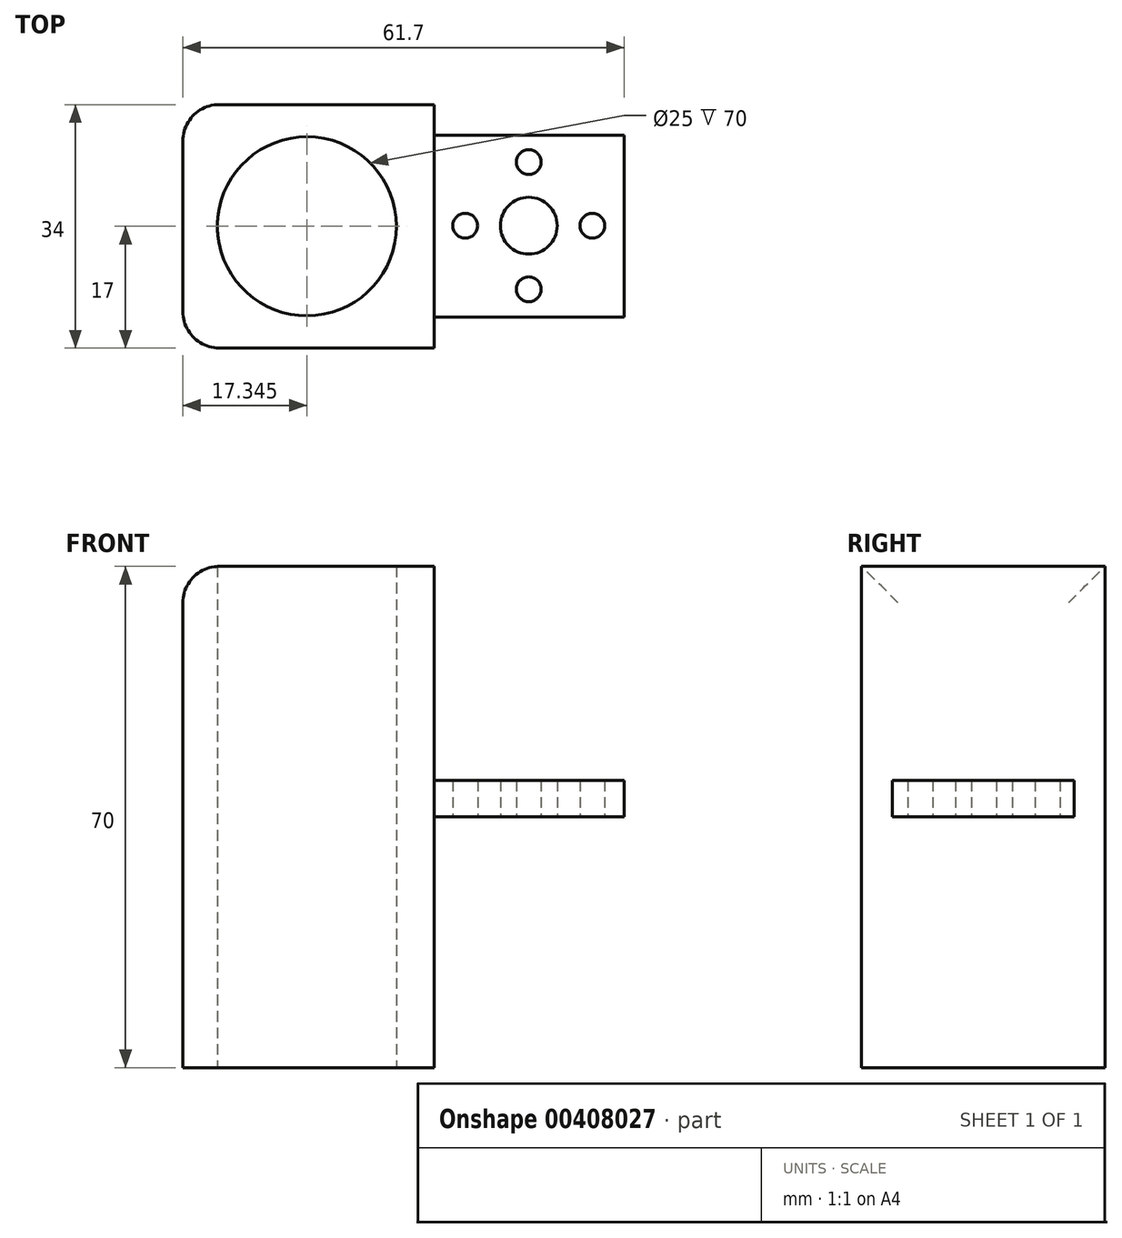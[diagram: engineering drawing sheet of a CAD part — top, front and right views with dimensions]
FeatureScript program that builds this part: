
annotation { "Feature Type Name" : "Feature", "Feature Type Description" : "" }
export const myFeature = defineFeature(function(context is Context, id is Id, definition is map)
    precondition{}
    {
        {
            var Q0;
            Q0=qCreatedBy(makeId("Top.planeOp"),FACE);
            var sketch = newSketch(context, id + "F0", { "sketchPlane" : qUnion([Q0])});
            skCircle(sketch, "E0", {"center": v(0, 0) * mm, "radius": 12.7 * mm});
            skLineSegment(sketch, "E1.bottom", {"start": v(12.38, 12.7) * mm, "end": v(42.86, 12.7) * mm});
            skLineSegment(sketch, "E1.top", {"start": v(12.38, -12.7) * mm, "end": v(42.86, -12.7) * mm});
            skLineSegment(sketch, "E1.right", {"start": v(42.86, 12.7) * mm, "end": v(42.86, -12.7) * mm});
            skCircle(sketch, "E2", {"center": v(29.5, 8.96) * mm, "radius": 1.74 * mm});
            skCircle(sketch, "E3", {"center": v(20.62, 0.08) * mm, "radius": 1.74 * mm});
            skCircle(sketch, "E4", {"center": v(38.38, 0.08) * mm, "radius": 1.74 * mm});
            skCircle(sketch, "E5", {"center": v(29.5, -8.8) * mm, "radius": 1.74 * mm});
            skCircle(sketch, "E6", {"center": v(29.5, 0.08) * mm, "radius": 3.97 * mm});
            skPoint(sketch, "E7", {"position": v(0, 12.7) * mm});
            skLineSegment(sketch, "E8", {"start": v(0, 12.7) * mm, "end": v(12.38, 12.7) * mm});
            skPoint(sketch, "E9", {"position": v(0, -12.7) * mm});
            skLineSegment(sketch, "E10", {"start": v(0, -12.7) * mm, "end": v(12.38, -12.7) * mm});
            skLineSegment(sketch, "E11", {"start": v(14.1, 12.7) * mm, "end": v(14.1, -12.7) * mm});
            skLineSegment(sketch, "E12.MirrorCS", {"start": v(0, 12.7) * mm, "end": v(-12.38, 12.7) * mm});
            skLineSegment(sketch, "E13.MirrorCS", {"start": v(-14.1, 12.7) * mm, "end": v(-14.1, -12.7) * mm});
            skLineSegment(sketch, "E14.MirrorCS", {"start": v(0, -12.7) * mm, "end": v(-12.38, -12.7) * mm});
            skLineSegment(sketch, "E15", {"start": v(-14.1, 12.7) * mm, "end": v(-12.38, 12.7) * mm});
            skLineSegment(sketch, "E16", {"start": v(-14.1, -12.7) * mm, "end": v(-12.38, -12.7) * mm});
            skLineSegment(sketch, "E17", {"start": v(14.1, 12.7) * mm, "end": v(14.1, 14.85) * mm});
            skLineSegment(sketch, "E18.MirrorCS", {"start": v(14.1, -12.7) * mm, "end": v(14.1, -14.85) * mm});
            skLineSegment(sketch, "E19", {"start": v(14.1, 14.85) * mm, "end": v(-14.1, 14.85) * mm});
            skLineSegment(sketch, "E20", {"start": v(-14.1, 14.85) * mm, "end": v(-14.1, 12.7) * mm});
            skLineSegment(sketch, "E21.MirrorCS", {"start": v(14.1, -14.85) * mm, "end": v(-14.1, -14.85) * mm});
            skLineSegment(sketch, "E22.MirrorCS", {"start": v(-14.1, -14.85) * mm, "end": v(-14.1, -12.7) * mm});
            skSolve(sketch);
        }
        {
            var Q0;
            {var subQ0=sQuery(id+"F0.wireOp",EDGE,"E1.right");Q0=makeQuery(id+"F0.imprint","IMPRINT",FACE,{"disambiguationData":[TD([[makeQuery(id+"F0.imprint","IMPRINT",EDGE,{"derivedFrom":subQ0}),-1.0]])]});}
            extrude(context, id + "F1", {"entities" : qUnion([Q0]), "depth" : 5.08 * mm, "offsetDistance" : 25.4 * mm});
        }
        {
            var Q0;
            Q0=qCreatedBy(makeId("Top.planeOp"),FACE);
            var sketch = newSketch(context, id + "F2", { "sketchPlane" : qUnion([Q0])});
            skPoint(sketch, "E23", {"position": v(0, -12.3) * mm});
            skLineSegment(sketch, "E24.right", {"start": v(-18.84, 17) * mm, "end": v(-18.84, -17) * mm});
            skPoint(sketch, "E24.middle", {"position": v(0, 0) * mm});
            skCircle(sketch, "E25", {"center": v(-1.5, 0) * mm, "radius": 12.5 * mm});
            skLineSegment(sketch, "E26", {"start": v(16.27, 17) * mm, "end": v(16.27, -17) * mm});
            skLineSegment(sketch, "E27", {"start": v(-18.84, 17) * mm, "end": v(16.27, 17) * mm});
            skLineSegment(sketch, "E28", {"start": v(-18.84, -17) * mm, "end": v(16.27, -17) * mm});
            skSolve(sketch);
        }
        {
            var Q0;
            Q0=makeQuery(id+"F2.imprint","IMPRINT",FACE,{"disambiguationData":[TD([[makeQuery(id+"F2.imprint","IMPRINT",EDGE,{"derivedFrom":sQuery(id+"F2.wireOp",EDGE,"E24.right")}),1.0]])]});
            extrude(context, id + "F3", {"entities" : qUnion([Q0]), "operationType" : NewBodyOperationType.ADD, "endBound" : BoundingType.SYMMETRIC, "depth" : 70 * mm, "offsetDistance" : 25.4 * mm});
        }
        {
            var Q0;
            Q0=makeQuery(id+"F3.opExtrude","CAP_EDGE",EDGE,{"disambiguationData":[OSD([sQuery(id+"F2.wireOp",EDGE,"E24.bottom")])],"isStart":false});
            var Q1;
            Q1=makeQuery(id+"F3.opExtrude","CAP_EDGE",EDGE,{"disambiguationData":[OSD([sQuery(id+"F2.wireOp",EDGE,"E24.right")])],"isStart":false});
            var Q2;
            Q2=makeQuery(id+"F3.opExtrude","CAP_EDGE",EDGE,{"disambiguationData":[OSD([sQuery(id+"F2.wireOp",EDGE,"E24.top")])],"isStart":false});
            var Q3;
            Q3=makeQuery(id+"F3.opExtrude","SWEPT_EDGE",EDGE,{"disambiguationData":[OSD([sQuery(id+"F2.wireOp",EDGE,"E24.bottom"),sQuery(id+"F2.wireOp",EDGE,"E24.right")])]});
            var Q4;
            Q4=makeQuery(id+"F3.opExtrude","SWEPT_EDGE",EDGE,{"disambiguationData":[OSD([sQuery(id+"F2.wireOp",EDGE,"E24.top"),sQuery(id+"F2.wireOp",EDGE,"E24.right")])]});
            fillet(context, id + "F4", {"entities" : qUnion([Q0, Q1, Q2, Q3, Q4]), "radius" : 5.08 * mm, "tangentPropagation" : true, "allowEdgeOverflow" : false});
        }
    });
